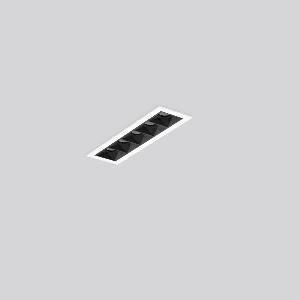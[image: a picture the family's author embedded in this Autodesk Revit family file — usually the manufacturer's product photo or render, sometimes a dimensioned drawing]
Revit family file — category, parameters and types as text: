
# Revit family: beamline_slim_641324_002_76_5c05
name_source: partatom
category: Lighting Fixtures
units: mm (PartAtom-declared; Revit-internal decimal feet)

## family parameters
Cut with Voids When Loaded = No
Host = Face
Light Source = No
Part Type = Normal
Room Calculation Point = No
Round Connector Dimension = Use Diameter
Shared = No

## types (1)
- BEAMLINE SLIM (1 x LED Modul 927, 940 lm, 2700)
    Apparent Load = 14 VA
    CIE Flux Codes = 100 100 100 100 100
    Color Rendering = 92
    Color Temperature = 2700
    Default Elevation = 1800 mm
    Description = Series: BEAMLINE SLIM
Minimalistic recessed ceiling luminaire for aesthetically sophisticated lighting. Housing: metal, powder-coated. Perfect heat management with an aluminium heat sink. LED light unit with MRS technology: Mini-Reflector-System made of metallised thermoplastic with prismatic black glare-suppressing frame for pleasant glare-free light (RUG < 10). Medium beam light distribution. Ceiling installation with spring system. Including separate LED converter with connecting cable 450 mm. 
Colour: traffic white, matt (RAL 9016)
Length: 155 mm
Width: 45 mm
Height: 1.5 mm
Cut-out length: 150 mm
Cut-out width: 40 mm
Recess height: 110 mm
Luminaire: recess height: 60 mm
Lamp: LED
Socket: without socket
Colour temperature: 2700K
Colour rendering index (CRI): 90
System power: 14 W
Rated luminous flux: 940 lm
Luminous efficiency: 67 lm/W
Control gear: Converter, dimmable, DALI
Protection class: II
Type of protection: IP 20
    Height = 0 mm  [stored 0 ft]
    Lamp = 1 x LED Modul 927
    Lamp Light Flux = 940 lm
    Lamp count = 1
    Length = 155 mm
    Lifetime = 50000 h
    Luminous efficacy = 67 lm/W
    Manufacturer = RZB
    ModVariant = No
    Model = 641324.002.76
    Mounting Place = Ceiling
    Mounting Type = Recessed
    Number of Poles = 1
    OnlyDefault = Yes
    Power Factor = 1
    Product Name = BEAMLINE SLIM
    Product group = Recessed LED linear luminaires
    ProductGroupID = 407
    Protection Class = Protection class II
    Protection Degree = IP 20
    RLX_Detail_Level = 1
    RLX_Emergency_Light_Flux = 0 lm
    RLX_Emergency_Type = 0
    RLX_Emergency_Type_DB = No
    RlxData = <blob elided: 11681 chars, md5=95039766>
    Socket = socket
    Standby Power = 0 W
    System Light Flux = 940 lm
    System Power = 14 W
    Type Comments = Product without accessories
    Type Image = 641323.002.jpg
    URL = http://relux.com
    VarID = ---
    Voltage = 230 V
    Voltage Range = 220-240 V
    Weight = 0.00 kg
    Width = 45 mm

note: [stored X ft] marks values corroborated as IEEE doubles in the binary element streams (Revit-internal decimal feet)

## geometry (parser evidence)
native form markers: Sweep x11
no freeform markers — native parametric forms only
